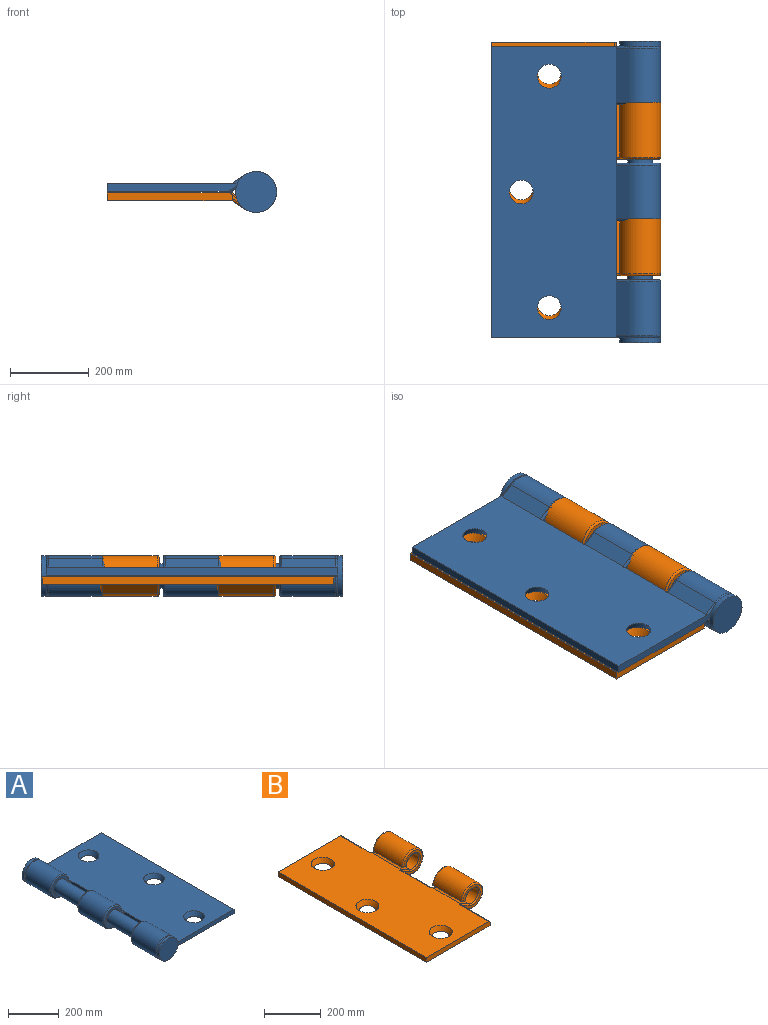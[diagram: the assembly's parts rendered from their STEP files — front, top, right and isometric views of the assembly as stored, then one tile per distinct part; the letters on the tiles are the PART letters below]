
ASSEMBLY  parts=2 mates=1
PART A: 57 faces, bbox 434.8x767.1x112.7 mm
  f0: plane 334.27x25mm, normal (0,-1,0), area 6570mm2, adj f10,f11,f12,f35,f37,f52
  f1: plane 137.16x45.58mm, normal (-0.48,0,0.87), area 7146.2mm2, adj f10,f27,f49,f51
  f2: plane 137.16x45.58mm, normal (-0.48,0,0.87), area 7146.2mm2, adj f10,f31,f39,f51
  f3: plane 137.16x32.94mm, normal (0.54,0,-0.84), area 5360.5mm2, adj f5,f12,f29,f47
  f4: plane 137.16x32.94mm, normal (0.54,0,-0.84), area 5360.5mm2, adj f6,f12,f33,f41
  f5: cylinder r=52.07mm len=137.16mm, axis (0,1,0), area 37713.3mm2, adj f3,f7,f28,f46
  f6: cylinder r=52.07mm len=137.16mm, axis (0,1,0), area 37713.3mm2, adj f4,f8,f32,f40
  f7: plane 147.32x20.32mm, normal (0,0,-1), area 2971.4mm2, adj f5,f25,f26,f28,f46,f48,f51,f54
  f8: plane 147.32x20.32mm, normal (0,0,-1), area 2971.4mm2, adj f6,f22,f24,f30,f32,f38,f40,f51
  f9: plane 137.16x45.58mm, normal (-0.48,0,0.87), area 7146.2mm2, adj f10,f35,f43,f51
  f10: plane 741.68x317.5mm, normal (0,0,1), area 219894.5mm2, adj f0,f1,f2,f9,f11,f16,f17,f18
  f11: plane 741.68x20.32mm, normal (1,0,0), area 15070.9mm2, adj f0,f10,f12,f16
  f12: plane 741.68x326.94mm, normal (0,0,-1), area 226748.1mm2, adj f0,f3,f4,f11,f13,f16,f17,f18
  f13: plane 137.16x32.94mm, normal (0.54,0,-0.84), area 5360.5mm2, adj f12,f14,f37,f45
  f14: cylinder r=52.07mm len=137.16mm, axis (0,1,0), area 37713.3mm2, adj f13,f15,f36,f44
  f15: plane 147.32x20.32mm, normal (0,0,-1), area 2971.4mm2, adj f14,f21,f34,f36,f42,f44,f50,f51
  f16: plane 334.27x25mm, normal (0,1,0), area 6570mm2, adj f10,f11,f12,f47,f49,f55
  f17: cone r=30.48mm half-angle=26.6deg, axis (0,0,1), area 5076mm2, adj f10,f12
  f18: cone r=30.48mm half-angle=26.6deg, axis (0,0,1), area 5076mm2, adj f10,f12
  f19: cone r=30.48mm half-angle=26.6deg, axis (0,0,1), area 5076mm2, adj f10,f12
  f20: plane 160.02x20.32mm, normal (-1,0,0), area 3071mm2, adj f10,f12,f21,f22,f31,f33,f43,f45
  f21: plane 107.95x93.98mm, normal (0,1,0), area 2636.3mm2, adj f15,f20,f42,f43,f44,f45
  f22: plane 107.95x93.98mm, normal (0,-1,0), area 2636.3mm2, adj f8,f20,f30,f31,f32,f33
  f23: plane 160.02x20.32mm, normal (-1,0,0), area 3071mm2, adj f10,f12,f24,f25,f27,f29,f39,f41
  f24: plane 107.95x93.98mm, normal (0,1,0), area 2636.3mm2, adj f8,f23,f38,f39,f40,f41
  f25: plane 107.95x93.98mm, normal (0,-1,0), area 2636.3mm2, adj f7,f23,f26,f27,f28,f29
  f26: torus R=36.83mm, axis (0,-1,0), area 1398.9mm2, adj f7,f25,f27,f51
  f27: cylinder r=5.08mm len=48.04mm, axis (0.87,0,0.48), area 407.6mm2, adj f1,f23,f25,f26
  f28: torus R=46.99mm, axis (0,-1,0), area 2116.3mm2, adj f5,f7,f25,f29
  f29: cylinder r=5.08mm len=38.41mm, axis (-0.84,0,-0.54), area 321.3mm2, adj f3,f23,f25,f28
  f30: torus R=36.83mm, axis (0,-1,0), area 1398.9mm2, adj f8,f22,f31,f51
  f31: cylinder r=5.08mm len=48.04mm, axis (0.87,0,0.48), area 407.6mm2, adj f2,f20,f22,f30
  f32: torus R=46.99mm, axis (0,-1,0), area 2116.3mm2, adj f6,f8,f22,f33
  f33: cylinder r=5.08mm len=38.41mm, axis (-0.84,0,-0.54), area 321.3mm2, adj f4,f20,f22,f32
  f34: torus R=36.83mm, axis (0,-1,0), area 1398.9mm2, adj f15,f35,f50,f51
  f35: cylinder r=5.08mm len=56.07mm, axis (-0.87,0,-0.48), area 442.4mm2, adj f0,f9,f10,f34,f50
  f36: torus R=46.99mm, axis (0,-1,0), area 2116.3mm2, adj f14,f15,f37,f50
  f37: cylinder r=5.08mm len=35.68mm, axis (0.84,0,0.54), area 288.8mm2, adj f0,f12,f13,f36,f50
  f38: torus R=36.83mm, axis (0,-1,0), area 1398.9mm2, adj f8,f24,f39,f51
  f39: cylinder r=5.08mm len=48.04mm, axis (-0.87,0,-0.48), area 407.6mm2, adj f2,f23,f24,f38
  f40: torus R=46.99mm, axis (0,-1,0), area 2116.3mm2, adj f6,f8,f24,f41
  f41: cylinder r=5.08mm len=38.41mm, axis (0.84,0,0.54), area 321.3mm2, adj f4,f23,f24,f40
  f42: torus R=36.83mm, axis (0,-1,0), area 1398.9mm2, adj f15,f21,f43,f51
  f43: cylinder r=5.08mm len=48.04mm, axis (-0.87,0,-0.48), area 407.6mm2, adj f9,f20,f21,f42
  f44: torus R=46.99mm, axis (0,-1,0), area 2116.3mm2, adj f14,f15,f21,f45
  f45: cylinder r=5.08mm len=38.41mm, axis (0.84,0,0.54), area 321.3mm2, adj f13,f20,f21,f44
  f46: torus R=46.99mm, axis (0,-1,0), area 2116.3mm2, adj f5,f7,f47,f54
  f47: cylinder r=5.08mm len=35.68mm, axis (-0.84,0,-0.54), area 288.8mm2, adj f3,f12,f16,f46,f54
  f48: torus R=36.83mm, axis (0,-1,0), area 1398.9mm2, adj f7,f49,f51,f54
  f49: cylinder r=5.08mm len=56.07mm, axis (0.87,0,0.48), area 442.4mm2, adj f1,f10,f16,f48,f54
  f50: plane 104.14x104.14mm, normal (0,1,0), area 2834.9mm2, adj f15,f34,f35,f36,f37,f51,f52
  f51: cylinder r=31.75mm len=741.68mm, axis (0,-1,0), area 79787.5mm2, adj f1,f2,f7,f8,f9,f15,f26,f30
  f52: cylinder r=52.07mm len=104.14mm, axis (0,1,0), area 4155mm2, adj f0,f50,f53
  f53: plane 104.14x104.14mm, normal (0,-1,0), area 8517.8mm2, adj f52
  f54: plane 104.14x104.14mm, normal (0,-1,0), area 2834.9mm2, adj f7,f46,f47,f48,f49,f51,f55
  f55: cylinder r=52.07mm len=104.14mm, axis (0,-1,0), area 4155mm2, adj f16,f54,f56
  f56: plane 104.14x104.14mm, normal (0,1,0), area 8517.8mm2, adj f55
PART B: 44 faces, bbox 434.8x741.7x112.7 mm
  f0: cylinder r=31.75mm len=139.7mm, axis (0,1,0), area 23144.5mm2, adj f2,f8,f33,f38
  f1: cylinder r=31.75mm len=139.7mm, axis (0,1,0), area 23144.5mm2, adj f3,f9,f35,f40
  f2: plane 139.7x45.58mm, normal (0.48,0,0.87), area 7278.5mm2, adj f0,f10,f34,f37
  f3: plane 139.7x45.58mm, normal (0.48,0,0.87), area 7278.5mm2, adj f1,f10,f36,f39
  f4: plane 139.7x32.94mm, normal (-0.54,0,-0.84), area 5459.8mm2, adj f6,f12,f26,f30
  f5: plane 139.7x32.94mm, normal (-0.54,0,-0.84), area 5459.8mm2, adj f7,f12,f28,f32
  f6: cylinder r=52.07mm len=139.7mm, axis (0,1,0), area 38411.7mm2, adj f4,f8,f25,f29
  f7: cylinder r=52.07mm len=139.7mm, axis (0,1,0), area 38411.7mm2, adj f5,f9,f27,f31
  f8: plane 149.86x20.32mm, normal (0,0,-1), area 3023mm2, adj f0,f6,f22,f24,f25,f29,f33,f38
  f9: plane 149.86x20.32mm, normal (0,0,-1), area 3023mm2, adj f1,f7,f19,f21,f27,f31,f35,f40
  f10: plane 741.68x317.5mm, normal (0,0,1), area 217631.5mm2, adj f2,f3,f11,f13,f14,f15,f16,f17
  f11: plane 741.68x20.32mm, normal (-1,0,0), area 15070.9mm2, adj f10,f12,f13,f14
  f12: plane 741.68x317.5mm, normal (0,0,-1), area 226727.5mm2, adj f4,f5,f11,f13,f14,f15,f16,f17
  f13: plane 317.5x20.32mm, normal (0,-1,0), area 6446.1mm2, adj f10,f11,f12,f23,f43
  f14: plane 317.5x20.32mm, normal (0,1,0), area 6446.1mm2, adj f10,f11,f12,f18,f42
  f15: cone r=30.48mm half-angle=26.6deg, axis (0,0,1), area 5076mm2, adj f10,f12
  f16: cone r=30.48mm half-angle=26.6deg, axis (0,0,1), area 5076mm2, adj f10,f12
  f17: cone r=30.48mm half-angle=26.6deg, axis (0,0,1), area 5076mm2, adj f10,f12
  f18: plane 152.4x15.24mm, normal (1,0,0), area 2251.7mm2, adj f12,f14,f19,f32,f39,f42
  f19: plane 107.95x93.98mm, normal (0,1,0), area 2636.3mm2, adj f9,f18,f31,f32,f39,f40
  f20: plane 157.48x15.24mm, normal (1,0,0), area 2258.3mm2, adj f12,f21,f22,f28,f30,f36,f37,f41
  f21: plane 107.95x93.98mm, normal (0,-1,0), area 2636.3mm2, adj f9,f20,f27,f28,f35,f36
  f22: plane 107.95x93.98mm, normal (0,1,0), area 2636.3mm2, adj f8,f20,f29,f30,f37,f38
  f23: plane 152.4x15.24mm, normal (1,0,0), area 2251.7mm2, adj f12,f13,f24,f26,f34,f43
  f24: plane 107.95x93.98mm, normal (0,-1,0), area 2636.3mm2, adj f8,f23,f25,f26,f33,f34
  f25: torus R=46.99mm, axis (0,1,0), area 2116.3mm2, adj f6,f8,f24,f26
  f26: cylinder r=5.08mm len=38.41mm, axis (-0.84,0,0.54), area 321.3mm2, adj f4,f23,f24,f25
  f27: torus R=46.99mm, axis (0,1,0), area 2116.3mm2, adj f7,f9,f21,f28
  f28: cylinder r=5.08mm len=38.41mm, axis (-0.84,0,0.54), area 321.3mm2, adj f5,f20,f21,f27
  f29: torus R=46.99mm, axis (0,1,0), area 2116.3mm2, adj f6,f8,f22,f30
  f30: cylinder r=5.08mm len=38.41mm, axis (0.84,0,-0.54), area 321.3mm2, adj f4,f20,f22,f29
  f31: torus R=46.99mm, axis (0,1,0), area 2116.3mm2, adj f7,f9,f19,f32
  f32: cylinder r=5.08mm len=38.41mm, axis (0.84,0,-0.54), area 321.3mm2, adj f5,f18,f19,f31
  f33: torus R=36.83mm, axis (0,1,0), area 1398.9mm2, adj f0,f8,f24,f34
  f34: cylinder r=5.08mm len=51.93mm, axis (0.87,0,-0.48), area 416.1mm2, adj f2,f10,f23,f24,f33,f43
  f35: torus R=36.83mm, axis (0,1,0), area 1398.9mm2, adj f1,f9,f21,f36
  f36: cylinder r=5.08mm len=51.93mm, axis (0.87,0,-0.48), area 416.1mm2, adj f3,f10,f20,f21,f35,f41
  f37: cylinder r=5.08mm len=51.93mm, axis (-0.87,0,0.48), area 416.1mm2, adj f2,f10,f20,f22,f38,f41
  f38: torus R=36.83mm, axis (0,1,0), area 1398.9mm2, adj f0,f8,f22,f37
  f39: cylinder r=5.08mm len=51.93mm, axis (-0.87,0,0.48), area 416.1mm2, adj f3,f10,f18,f19,f40,f42
  f40: torus R=36.83mm, axis (0,1,0), area 1398.9mm2, adj f1,f9,f19,f39
  f41: cylinder r=5.08mm len=149.68mm, axis (0,1,0), area 1188mm2, adj f10,f20,f36,f37
  f42: cylinder r=5.08mm len=148.5mm, axis (0,1,0), area 1181.8mm2, adj f10,f14,f18,f39
  f43: cylinder r=5.08mm len=148.5mm, axis (0,1,0), area 1181.8mm2, adj f10,f13,f23,f34
PLACE A rot(axis=(0,1,0),180deg) t=(-11,-77.89,71.1)mm
PLACE B t=(-133.97,-67.73,25.38)mm
MATE revolute A.f5 <-> B.f0  axis (0,1,0) through (-73.01,-220.13,48.24)mm
